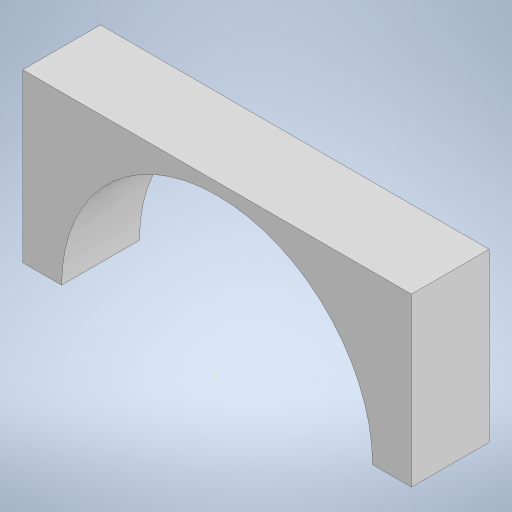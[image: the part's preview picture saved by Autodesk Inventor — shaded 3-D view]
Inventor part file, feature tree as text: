
AUTODESK INVENTOR PART (.ipt)
format: ipt  version: 2023 (Build 270158000, 158)  size: 214,528 bytes
history: native  units: mm
features: sketch x3, extrude x2
ambient origin geometry x8: Origin, YZ Plane, XZ Plane, XY Plane, X Axis, Y Axis, Z Axis, Center Point
bodies: Body1 (feature_tree)
feature tree (5):
  extrude  "Extrusion11"  Depth=43.0mm
  extrude  "Extrusion12"  Depth=20.0mm
  sketch  "Sketch15"  dims[d47=50.0mm d48=0.0mm]
  sketch  "Sketch13"  dims[d42=100.0mm d43=43.0mm]
  sketch  "Sketch14"  dims[d44=20.0mm d45=0.0mm d46=80.0mm]
